# Revit family: hangover_plug_30_shine_810-0442
name_source: partatom
category: Leuchten
revit_build: Autodesk Revit 2016 (Build: 20190508_0715(x64)
units: mm (PartAtom-declared; Revit-internal decimal feet)

## family parameters
Basisbauteil = Fläche
Beim Laden mit Abzugskörper schneiden = Nein
Bemaßung runder Anschluss = Durchmesser verwenden
Gemeinsam genutzt = Nein
Lichtquelle = Nein
Raumberechnungspunkt = Nein
Teiletyp = Normal

## types (1)
- 810-0442-I24-L00 (1 x LED, 455.22 lm, 6.5 W, 2700K)
    Beschreibung = HANGOVER PLUG 30 SHINE
    CIE Flux Codes = 99 100 100 100 85
    Color Rendering = 1A/90…99
    Color Temperature = 2700K
    Height = 450 mm
    Hersteller = Prolicht
    Lamp Light Flux = 455.22 lm
    Lamp Power = 6.5 W
    Lamp count = 1
    Lampe = 1 x LED
    Length = 28 mm
    Luminous efficacy = 60 lm/W
    ModVariant = Nein
    Modell = 810-0442
    Mounting Place = Ceiling
    Mounting Type = Pendant
    Number of Poles = 1
    OnlyDefault = Ja
    Power Factor = 1
    Product Name = HANGOVER PLUG 30 SHINE
    Product group = Suspended spotlights
    ProductGroupID = 942
    Protection Class = Protection class
    Protection Degree = Degree of protection
    RLX_Detail_Level = 1
    RlxData = <blob elided: 53581 chars, md5=b6838d35>
    Scheinlast = 7 VA
    Socket = socket
    Standby Power = 0 W
    System Light Flux = 389 lm
    System Power = 7 W
    Typenbild = 810-0442.jpg
    Typenkommentare = LENSE 24° (24),SHINE RING ABSICHTLICH_LEER (00)
    URL = http://relux.com
    VarID = 810-0442-i24-l00
    Voltage = 0 V
    Vorgabe-Ansicht = 1800 mm
    Weight = 0.00 kg
    Width = 0 mm  [stored 0 ft]

note: [stored X ft] marks values corroborated as IEEE doubles in the binary element streams (Revit-internal decimal feet)

## geometry (parser evidence)
native form markers: Blend x4, Sweep x13
no freeform markers — native parametric forms only
